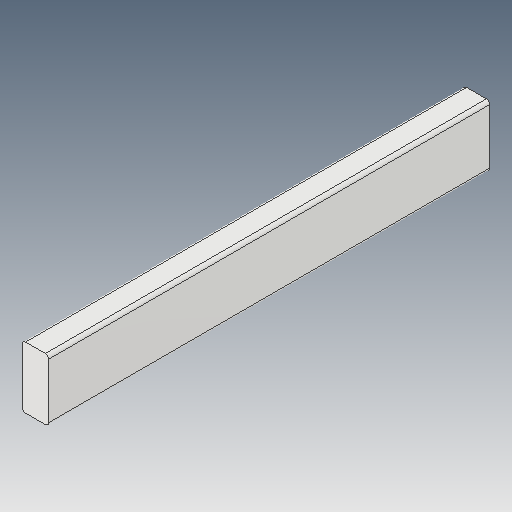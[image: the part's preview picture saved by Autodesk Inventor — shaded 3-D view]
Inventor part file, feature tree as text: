
AUTODESK INVENTOR PART (.ipt)
format: ipt  version: 2023.5 (Build 275446000, 446)  size: 87,040 bytes
history: native  units: in
note: dims shown in document units (in); Inventor stores cm internally (conversion verified against a paired STEP export)
features: fillet x1
ambient origin geometry x8: Origin, YZ Plane, XZ Plane, XY Plane, X Axis, Y Axis, Z Axis, Center Point
bodies: Solid1 (feature_tree)
feature tree (1):
  fillet  "Fillet1"  [1 undecoded]
note: 1 required parameter value undecoded (feature->parameter linkage not recoverable at this tier; creation-order binding heuristic only, values carry confidence <= 0.55)
